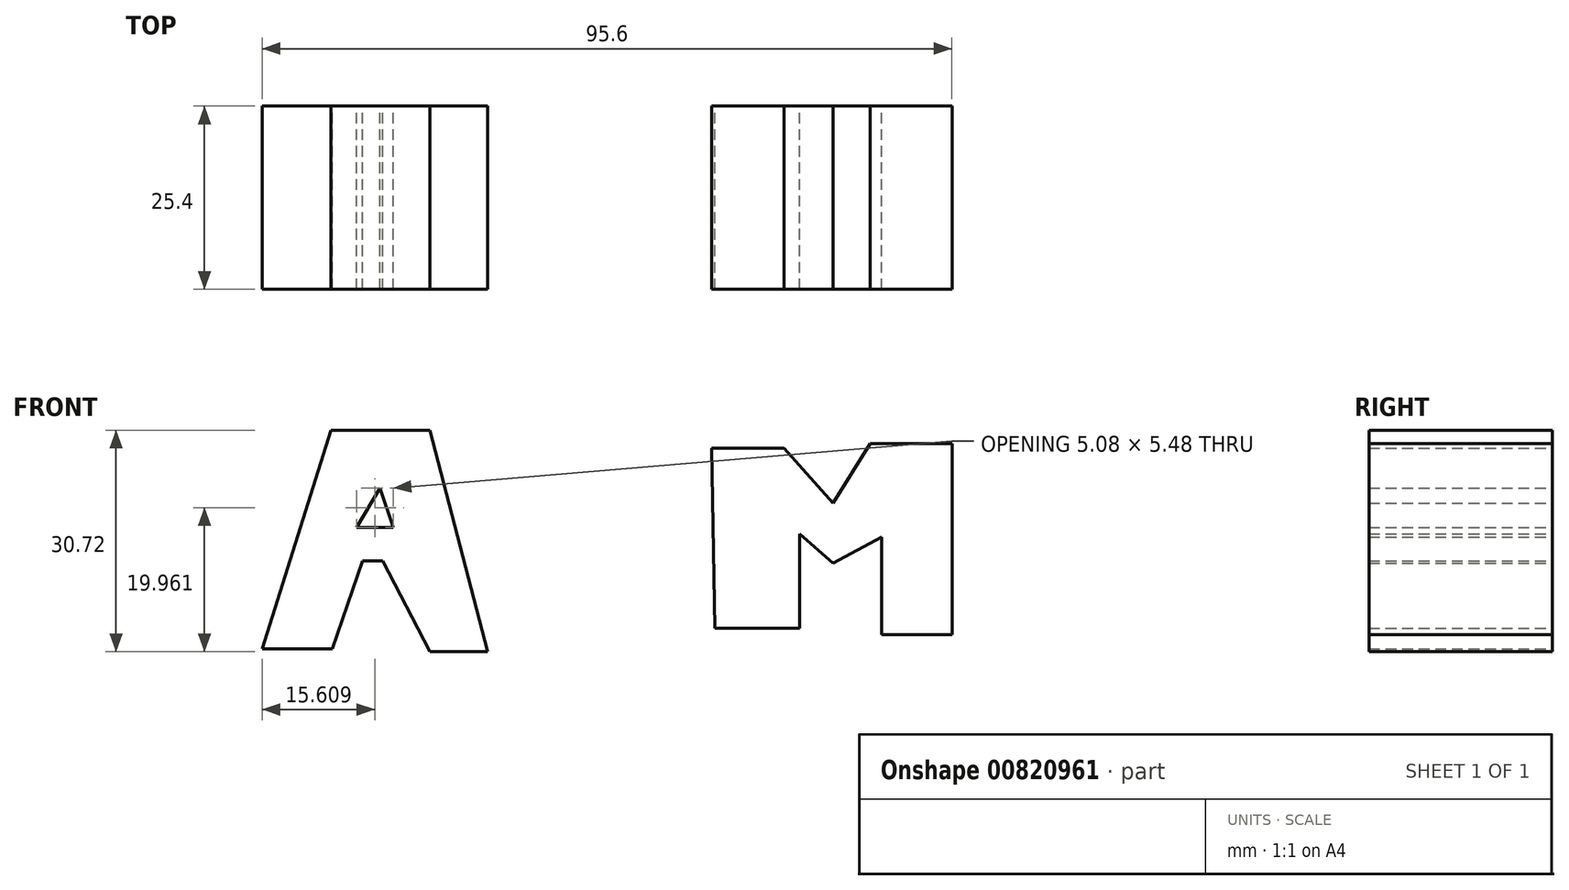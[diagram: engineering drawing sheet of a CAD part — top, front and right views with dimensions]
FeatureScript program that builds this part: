
annotation { "Feature Type Name" : "Feature", "Feature Type Description" : "" }
export const myFeature = defineFeature(function(context is Context, id is Id, definition is map)
    precondition{}
    {
        {
            var Q0;
            Q0=qCreatedBy(makeId("Front.planeOp"),FACE);
            var sketch = newSketch(context, id + "F0", { "sketchPlane" : qUnion([Q0])});
            skPoint(sketch, "E0.middle", {"position": v(-36.75, 26.63) * mm});
            skLineSegment(sketch, "E1", {"start": v(-43.91, 44.77) * mm, "end": v(-30.2, 44.77) * mm});
            skLineSegment(sketch, "E2", {"start": v(-30.2, 44.77) * mm, "end": v(-22.18, 14.05) * mm});
            skLineSegment(sketch, "E3", {"start": v(-22.18, 14.05) * mm, "end": v(-30.2, 14.05) * mm});
            skLineSegment(sketch, "E4", {"start": v(-30.2, 14.05) * mm, "end": v(-36.75, 26.63) * mm});
            skLineSegment(sketch, "E5", {"start": v(-36.75, 26.63) * mm, "end": v(-39.55, 26.63) * mm});
            skLineSegment(sketch, "E6", {"start": v(-39.55, 26.63) * mm, "end": v(-43.69, 14.48) * mm});
            skLineSegment(sketch, "E7", {"start": v(-43.69, 14.48) * mm, "end": v(-53.43, 14.48) * mm});
            skLineSegment(sketch, "E8", {"start": v(-53.43, 14.48) * mm, "end": v(-43.91, 44.77) * mm});
            skLineSegment(sketch, "E9", {"start": v(-35.28, 31.27) * mm, "end": v(-40.36, 31.27) * mm});
            skLineSegment(sketch, "E10", {"start": v(-40.36, 31.27) * mm, "end": v(-37.11, 36.75) * mm});
            skLineSegment(sketch, "E11", {"start": v(-37.11, 36.75) * mm, "end": v(-35.28, 31.27) * mm});
            skSolve(sketch);
        }
        {
            var Q0;
            Q0 = qSketchRegion(id + "F0", true);
            extrude(context, id + "F1", {"entities" : qUnion([Q0]), "depth" : 25.4 * mm, "offsetDistance" : 25.4 * mm});
        }
        {
            var Q0;
            Q0=qCreatedBy(makeId("Front.planeOp"),FACE);
            var sketch = newSketch(context, id + "F2", { "sketchPlane" : qUnion([Q0])});
            skPoint(sketch, "E12.middle", {"position": v(24.65, 29.08) * mm});
            skLineSegment(sketch, "E13", {"start": v(8.86, 42.3) * mm, "end": v(18.91, 42.3) * mm});
            skLineSegment(sketch, "E14", {"start": v(18.91, 42.3) * mm, "end": v(25.66, 34.66) * mm});
            skLineSegment(sketch, "E15", {"start": v(25.66, 34.66) * mm, "end": v(30.8, 42.87) * mm});
            skLineSegment(sketch, "E16", {"start": v(30.8, 42.87) * mm, "end": v(42.17, 42.87) * mm});
            skLineSegment(sketch, "E17", {"start": v(42.17, 42.87) * mm, "end": v(42.17, 16.45) * mm});
            skLineSegment(sketch, "E18", {"start": v(42.17, 16.45) * mm, "end": v(32.41, 16.45) * mm});
            skLineSegment(sketch, "E19", {"start": v(32.41, 16.45) * mm, "end": v(32.41, 29.95) * mm});
            skLineSegment(sketch, "E20", {"start": v(32.41, 29.95) * mm, "end": v(25.66, 26.36) * mm});
            skLineSegment(sketch, "E21", {"start": v(25.66, 26.36) * mm, "end": v(21.07, 30.38) * mm});
            skLineSegment(sketch, "E22", {"start": v(21.07, 30.38) * mm, "end": v(21.07, 17.31) * mm});
            skLineSegment(sketch, "E23", {"start": v(21.07, 17.31) * mm, "end": v(9.3, 17.31) * mm});
            skLineSegment(sketch, "E24", {"start": v(9.3, 17.31) * mm, "end": v(8.86, 42.3) * mm});
            skSolve(sketch);
        }
        {
            var Q0;
            Q0 = qSketchRegion(id + "F2", true);
            extrude(context, id + "F3", {"entities" : qUnion([Q0]), "depth" : 25.4 * mm, "offsetDistance" : 25.4 * mm});
        }
    });
